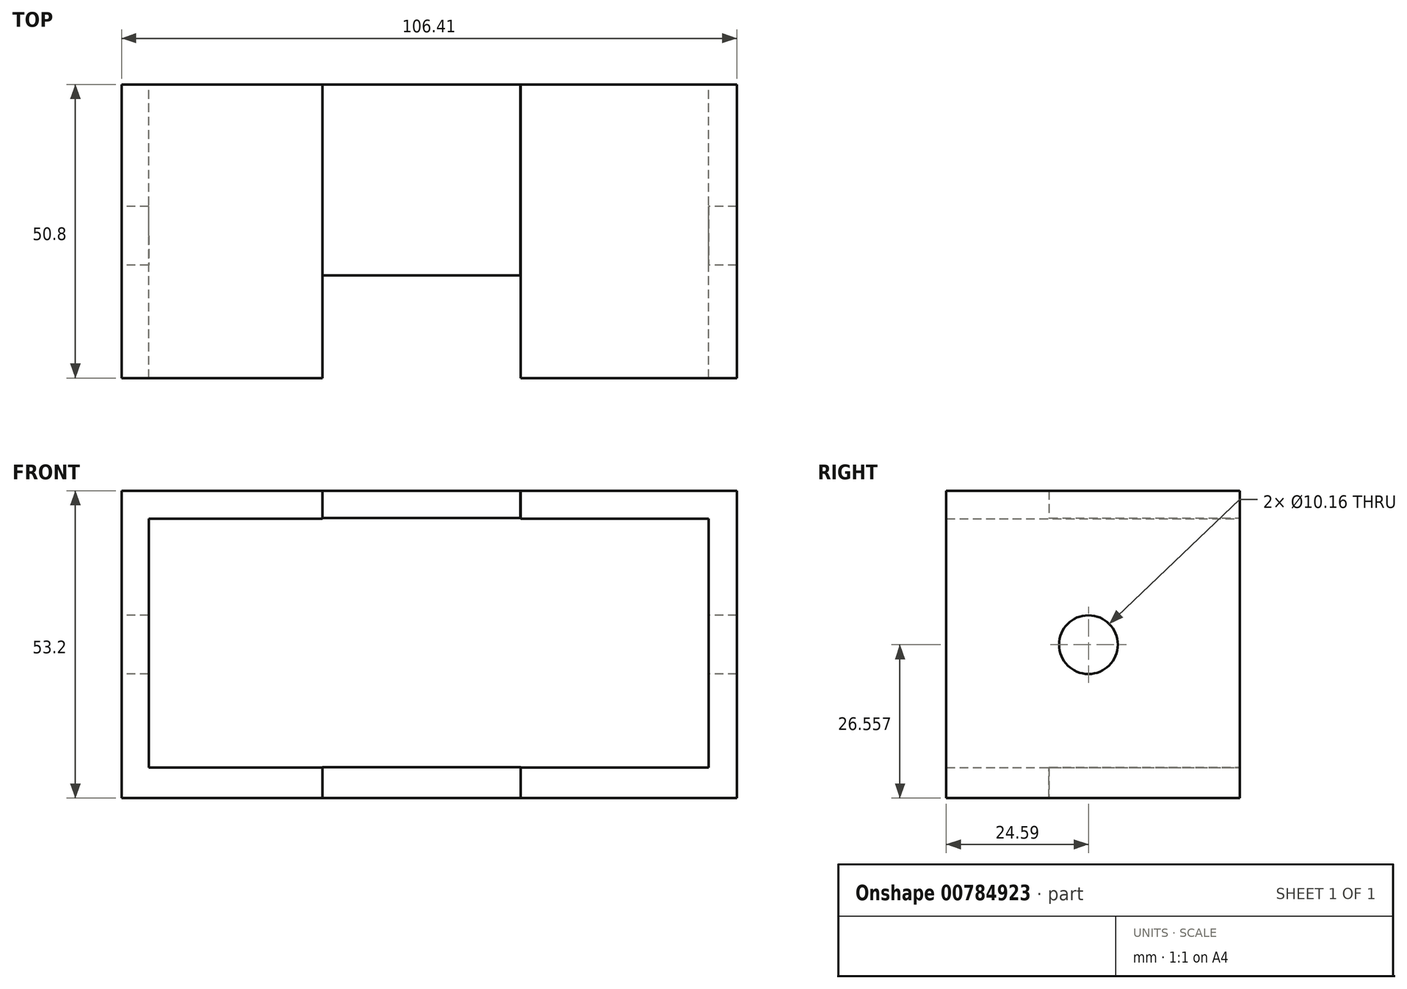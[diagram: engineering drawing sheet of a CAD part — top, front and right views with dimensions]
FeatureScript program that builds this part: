
annotation { "Feature Type Name" : "Feature", "Feature Type Description" : "" }
export const myFeature = defineFeature(function(context is Context, id is Id, definition is map)
    precondition{}
    {
        {
            var Q0;
            Q0=qCreatedBy(makeId("Front.planeOp"),FACE);
            var sketch = newSketch(context, id + "F0", { "sketchPlane" : qUnion([Q0])});
            skLineSegment(sketch, "E0.left", {"start": v(-64.48, 29.14) * mm, "end": v(-64.48, -24.06) * mm});
            skLineSegment(sketch, "E0.right", {"start": v(41.93, 29.14) * mm, "end": v(41.93, -24.06) * mm});
            skLineSegment(sketch, "E1.left", {"start": v(-59.8, 24.27) * mm, "end": v(-59.8, -18.78) * mm});
            skLineSegment(sketch, "E1.right", {"start": v(37.06, 24.27) * mm, "end": v(37.06, -18.78) * mm});
            skLineSegment(sketch, "E2", {"start": v(-64.48, 29.14) * mm, "end": v(-29.76, 29.14) * mm});
            skLineSegment(sketch, "E3", {"start": v(-59.8, 24.27) * mm, "end": v(-29.76, 24.27) * mm});
            skLineSegment(sketch, "E4", {"start": v(4.56, 29.14) * mm, "end": v(41.93, 29.14) * mm});
            skLineSegment(sketch, "E5", {"start": v(4.56, 24.27) * mm, "end": v(37.06, 24.27) * mm});
            skLineSegment(sketch, "E6", {"start": v(-59.8, -18.78) * mm, "end": v(-29.76, -18.78) * mm});
            skLineSegment(sketch, "E7", {"start": v(-29.76, -24.06) * mm, "end": v(-64.48, -24.06) * mm});
            skLineSegment(sketch, "E8", {"start": v(4.56, -18.78) * mm, "end": v(37.06, -18.78) * mm});
            skLineSegment(sketch, "E9", {"start": v(41.93, -24.06) * mm, "end": v(4.56, -24.06) * mm});
            skLineSegment(sketch, "E10", {"start": v(-29.76, 29.14) * mm, "end": v(-29.76, 24.27) * mm});
            skLineSegment(sketch, "E11", {"start": v(4.56, 29.14) * mm, "end": v(4.56, 24.27) * mm});
            skLineSegment(sketch, "E12", {"start": v(-29.76, -18.78) * mm, "end": v(-29.76, -24.06) * mm});
            skLineSegment(sketch, "E13", {"start": v(4.56, -18.78) * mm, "end": v(4.56, -24.06) * mm});
            skSolve(sketch);
        }
        {
            var Q0;
            Q0 = qSketchRegion(id + "F0", true);
            extrude(context, id + "F1", {"entities" : qUnion([Q0]), "depth" : 50.8 * mm, "offsetDistance" : 25.4 * mm});
        }
        {
            var Q0;
            Q0=qCreatedBy(makeId("Front.planeOp"),FACE);
            var sketch = newSketch(context, id + "F2", { "sketchPlane" : qUnion([Q0])});
            skLineSegment(sketch, "E14.bottom", {"start": v(4.55, -24.02) * mm, "end": v(-29.76, -24.02) * mm});
            skLineSegment(sketch, "E14.top", {"start": v(4.55, -18.72) * mm, "end": v(-29.76, -18.72) * mm});
            skLineSegment(sketch, "E14.left", {"start": v(4.55, -24.02) * mm, "end": v(4.55, -18.72) * mm});
            skLineSegment(sketch, "E14.right", {"start": v(-29.76, -24.02) * mm, "end": v(-29.76, -18.72) * mm});
            skLineSegment(sketch, "E15.bottom", {"start": v(-29.76, 29.1) * mm, "end": v(4.5, 29.1) * mm});
            skLineSegment(sketch, "E15.top", {"start": v(-29.76, 24.4) * mm, "end": v(4.5, 24.4) * mm});
            skLineSegment(sketch, "E15.left", {"start": v(-29.76, 29.1) * mm, "end": v(-29.76, 24.4) * mm});
            skLineSegment(sketch, "E15.right", {"start": v(4.5, 29.1) * mm, "end": v(4.5, 24.4) * mm});
            skSolve(sketch);
        }
        {
            var Q0;
            Q0 = qSketchRegion(id + "F2", true);
            extrude(context, id + "F3", {"entities" : qUnion([Q0]), "operationType" : NewBodyOperationType.ADD, "depth" : 33.02 * mm, "offsetDistance" : 25.4 * mm});
        }
        {
            var Q0;
            Q0=makeQuery(id+"F1.opExtrude","SWEPT_FACE",FACE,{"disambiguationData":[OSD([sQuery(id+"F0.wireOp",EDGE,"E0.left")])]});
            var sketch = newSketch(context, id + "F4", { "sketchPlane" : qUnion([Q0])});
            skCircle(sketch, "E16", {"center": v(26.2, 2.5) * mm, "radius": 5.68 * mm});
            skSolve(sketch);
        }
        {
            var Q0;
            Q0=sQuery(id+"F4.wireOp",VERTEX,"E16.center");
            var Q1;
            Q1=makeQuery(id+"F1.opExtrude","SWEPT_BODY",BODY,{"disambiguationData":[OSD([sQuery(id+"F0.wireOp",EDGE,"E0.left"),sQuery(id+"F0.wireOp",EDGE,"E1.left"),sQuery(id+"F0.wireOp",EDGE,"E2"),sQuery(id+"F0.wireOp",EDGE,"E3"),sQuery(id+"F0.wireOp",EDGE,"E6"),sQuery(id+"F0.wireOp",EDGE,"E7"),sQuery(id+"F0.wireOp",EDGE,"E10"),sQuery(id+"F0.wireOp",EDGE,"E12")])]});
            var Q2;
            Q2=makeQuery(id+"F1.opExtrude","SWEPT_BODY",BODY,{"disambiguationData":[OSD([sQuery(id+"F0.wireOp",EDGE,"E0.right"),sQuery(id+"F0.wireOp",EDGE,"E1.right"),sQuery(id+"F0.wireOp",EDGE,"E4"),sQuery(id+"F0.wireOp",EDGE,"E5"),sQuery(id+"F0.wireOp",EDGE,"E8"),sQuery(id+"F0.wireOp",EDGE,"E9"),sQuery(id+"F0.wireOp",EDGE,"E11"),sQuery(id+"F0.wireOp",EDGE,"E13")])]});
            hole(context, id + "F5", {"style" : HoleStyle.SIMPLE, "endStyle" : HoleEndStyle.THROUGH, "holeDiameter" : 10.16 * mm, "majorDiameter" : 6.35 * mm, "isTappedThrough" : true, "tappedDepth" : 12.7 * mm, "tapClearance" : 3, "locations" : qUnion([Q0]), "scope" : qUnion([Q1, Q2])});
        }
    });
